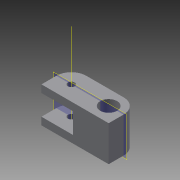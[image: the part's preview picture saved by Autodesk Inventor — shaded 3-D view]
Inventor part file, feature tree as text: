
AUTODESK INVENTOR PART (.ipt)
format: ipt  version: 2015 (Build 190159000, 159)  size: 122,880 bytes
history: native  units: mm
features: sketch x4, hole x2, extrude x1, plane x1, other x1, revolve x1
ambient origin geometry x8: Origin, YZ Plane, XZ Plane, XY Plane, X Axis, Y Axis, Z Axis, Center Point
bodies: Solid1 (feature_tree)
feature tree (10):
  extrude  "Extrusion1"  Depth=36.0mm
  hole  "Hole1"  [1 undecoded]
  hole  "Hole2"  [1 undecoded]
  plane  "Work Plane1"
  other  "Work Axis1"
  revolve  "Revolution2"  [1 undecoded]
  sketch  "Sketch1"  dims[d0=16.0mm d2=36.0mm]
  sketch  "Sketch2"  dims[d3=19.0mm d4=0.0mm d5=8.0mm]
  sketch  "Sketch3"  dims[d6=8.0mm]
  sketch  "Sketch7"  dims[d9=3.6mm d10=6.0mm d11=4.0mm d12=2.0mm d13=90.0deg d14=8.0mm d15=20.594885mm d16=8.0mm d17=8.0mm d18=9.0mm d19=6.0mm d20=4.0mm d21=2.0mm d22=90.0deg d23=8.0mm d24=20.594885mm d32=12.0mm d34=9.5mm d35=11.0mm d36=90.0deg]
note: 3 required parameter values undecoded (feature->parameter linkage not recoverable at this tier; creation-order binding heuristic only, values carry confidence <= 0.55)